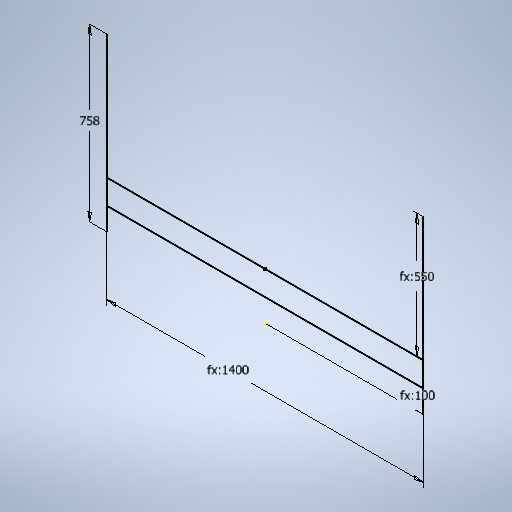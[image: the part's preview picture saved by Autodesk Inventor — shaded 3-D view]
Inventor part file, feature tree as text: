
AUTODESK INVENTOR PART (.ipt)
format: ipt  version: 2025 (Build 290162010, 162A)  size: 262,656 bytes
history: native  units: mm
features: sketch x1
ambient origin geometry x8: Origin, YZ Plane, XZ Plane, XY Plane, X Axis, Y Axis, Z Axis, Center Point
feature tree (1):
  sketch  "Sketch1"  dims[d0=758.0mm d1=1400.0mm d2=100.0mm d4=550.0mm]
